# Revit family: Series Blauberg Ultra
name_source: partatom
category: Mechanical Equipment
units: mm (PartAtom-declared; Revit-internal decimal feet)

## family parameters
Always vertical = Yes
Cut with Voids When Loaded = No
OmniClass Number = 23.75.00.00
OmniClass Title = Climate Control (HVAC)
Part Type = Normal
Room Calculation Point = No
Round Connector Dimension = Use Diameter
Shared = No
Work Plane-Based = No

## types (1)
- Series Blauberg Ultra 250
    00_20_Manufacturer = Blauberg
    00_20_Name = Ventilator
    00_20_Type = Series Blauberg Ultra 250
    Amperage = 0 A
    Default Elevation = 0 mm  [stored 0 ft]
    Frequency = 50 Hz
    Load Classification = HVAC
    Material = Plastic, opaque, white
    Maximum Air Flow = 482.0 m³/h
    Number of Fase = 1
    Power = 57 W
    Sound pressure level at 3 m distance = 36 dBA
    Voltage = 240 V
    Weight = 1.00 kg
    a = 198 mm  [stored 0.649606 ft]
    b = 38 mm  [stored 0.124672 ft]
    c = 330 mm  [stored 1.08268 ft]
    d = 148 mm  [stored 0.485564 ft]
    d1 = 142 mm  [stored 0.465879 ft]

note: [stored X ft] marks values corroborated as IEEE doubles in the binary element streams (Revit-internal decimal feet)

## geometry (parser evidence)
native form markers: Sweep x13
no freeform markers — native parametric forms only
